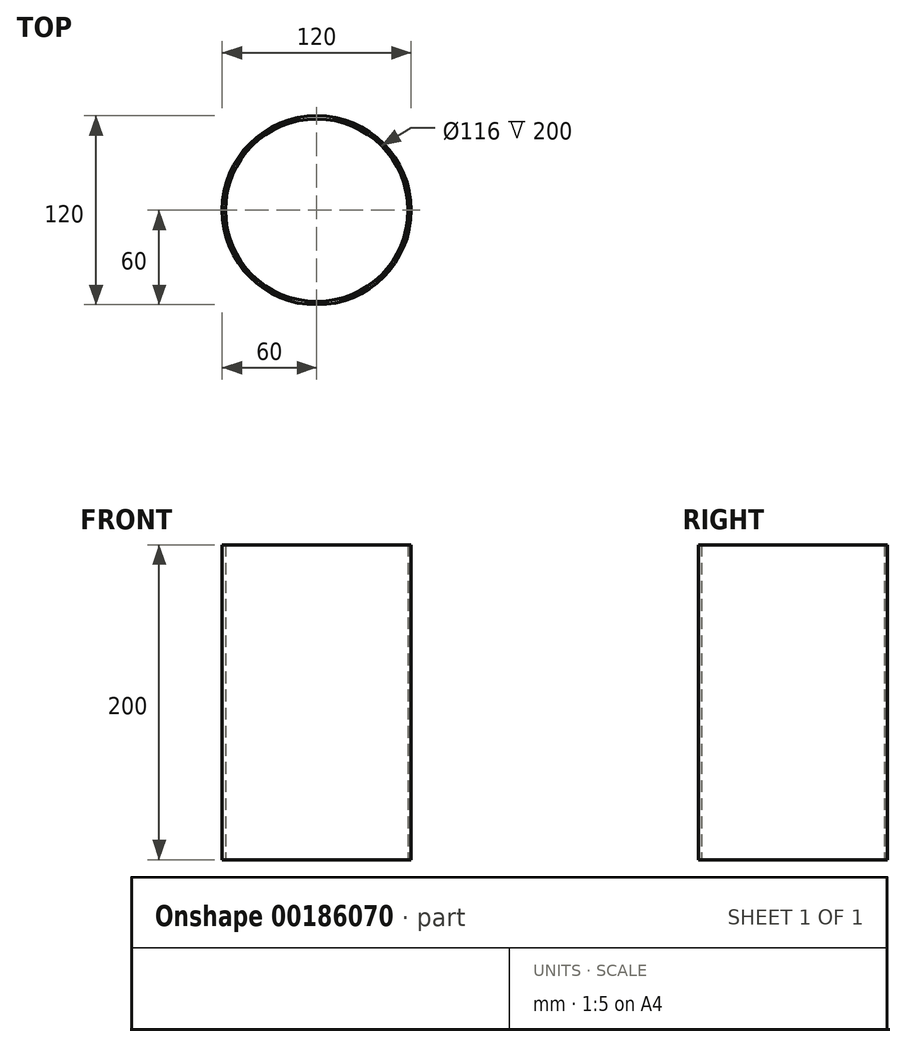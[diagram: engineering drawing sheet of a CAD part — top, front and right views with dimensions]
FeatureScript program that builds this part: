
annotation { "Feature Type Name" : "Feature", "Feature Type Description" : "" }
export const myFeature = defineFeature(function(context is Context, id is Id, definition is map)
    precondition{}
    {
        {
            var Q0;
            Q0=qCreatedBy(makeId("Top.planeOp"),FACE);
            var sketch = newSketch(context, id + "F0", { "sketchPlane" : qUnion([Q0])});
            skCircle(sketch, "E0", {"center": v(0, 0) * mm, "radius": 60 * mm});
            skCircle(sketch, "E1", {"center": v(0, 0) * mm, "radius": 58 * mm});
            skSolve(sketch);
        }
        {
            var Q0;
            Q0=makeQuery(id+"F0.imprint","IMPRINT",FACE,{"disambiguationData":[TD([[makeQuery(id+"F0.imprint","IMPRINT",EDGE,{"derivedFrom":sQuery(id+"F0.wireOp",EDGE,"E0")}),1.0]])]});
            extrude(context, id + "F1", {"entities" : qUnion([Q0]), "depth" : 200 * mm});
        }
    });
